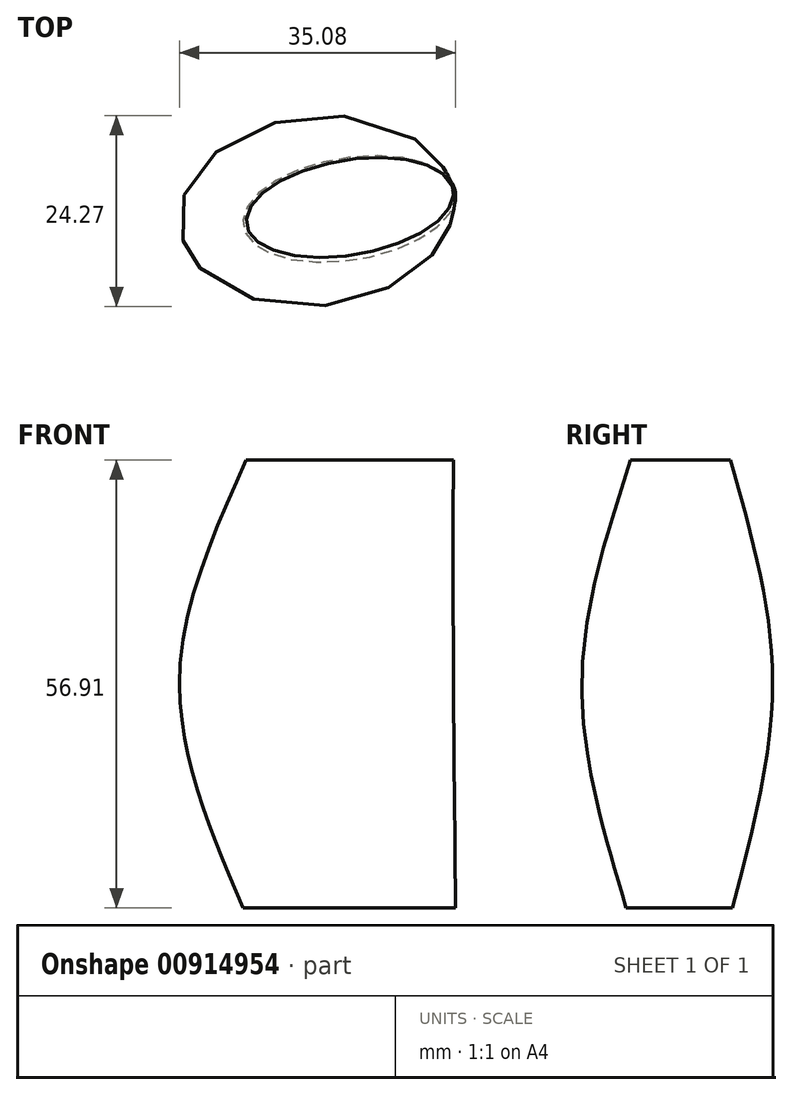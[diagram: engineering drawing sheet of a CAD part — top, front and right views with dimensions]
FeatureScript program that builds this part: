
annotation { "Feature Type Name" : "Feature", "Feature Type Description" : "" }
export const myFeature = defineFeature(function(context is Context, id is Id, definition is map)
    precondition{}
    {
        {
            var Q0;
            Q0=qCreatedBy(makeId("Front.planeOp"),FACE);
            var sketch = newSketch(context, id + "F0", { "sketchPlane" : qUnion([Q0])});
            skLineSegment(sketch, "E0", {"start": v(0, 69.9) * mm, "end": v(0, -51.9) * mm});
            skPoint(sketch, "E1", {"position": v(0, 56.91) * mm});
            skPoint(sketch, "E2", {"position": v(0, 0) * mm});
            skPoint(sketch, "E3", {"position": v(0, 29.5) * mm});
            skSolve(sketch);
        }
        {
            var Q0;
            Q0=qCreatedBy(makeId("Top.planeOp"),FACE);
            var sketch = newSketch(context, id + "F1", { "sketchPlane" : qUnion([Q0])});
            skEllipse(sketch, "E4", {"center": v(-10.4, 27.5) * mm, "majorRadius": 13.65 * mm, "minorRadius": 6.48 * mm, "majorAxis": v(0.99, 0.16)});
            skSolve(sketch);
        }
        {
            var Q0;
            Q0=sQuery(id+"F0.wireOp",VERTEX,"E3");
            var Q1;
            Q1=sQuery(id+"F0.wireOp",EDGE,"E0");
            cPlane(context, id + "F2", {"entities" : qUnion([Q0, Q1]), "cplaneType" : CPlaneType.CURVE_POINT, "offset" : 25.4 * mm, "width" : 152.4 * mm, "height" : 152.4 * mm});
        }
        {
            var Q0;
            Q0=sQuery(id+"F0.wireOp",VERTEX,"E1");
            var Q1;
            Q1=sQuery(id+"F0.wireOp",EDGE,"E0");
            cPlane(context, id + "F3", {"entities" : qUnion([Q0, Q1]), "cplaneType" : CPlaneType.CURVE_POINT, "offset" : 25.4 * mm, "width" : 152.4 * mm, "height" : 152.4 * mm});
        }
        {
            var Q0;
            Q0=qCreatedBy(id+"F2.planeOp",FACE);
            var sketch = newSketch(context, id + "F4", { "sketchPlane" : qUnion([Q0])});
            skEllipse(sketch, "E5", {"center": v(-14.56, -27.23) * mm, "majorRadius": 17.45 * mm, "minorRadius": 12.04 * mm, "majorAxis": v(1, -0.11)});
            skSolve(sketch);
        }
        {
            var Q0;
            Q0=qCreatedBy(id+"F3.planeOp",FACE);
            var sketch = newSketch(context, id + "F5", { "sketchPlane" : qUnion([Q0])});
            skEllipse(sketch, "E6", {"center": v(-10.33, -27.67) * mm, "majorRadius": 13.3 * mm, "minorRadius": 6.03 * mm, "majorAxis": v(0.99, -0.17)});
            skSolve(sketch);
        }
        {
            var Q0;
            Q0=makeQuery(id+"F5.imprint","IMPRINT",FACE,{"disambiguationData":[TD([[makeQuery(id+"F5.imprint","IMPRINT",EDGE,{"derivedFrom":sQuery(id+"F5.wireOp",EDGE,"E6")}),1.0]])]});
            var Q1;
            Q1=makeQuery(id+"F4.imprint","IMPRINT",FACE,{"disambiguationData":[TD([[makeQuery(id+"F4.imprint","IMPRINT",EDGE,{"derivedFrom":sQuery(id+"F4.wireOp",EDGE,"E5")}),1.0]])]});
            var Q2;
            Q2=makeQuery(id+"F1.imprint","IMPRINT",FACE,{"disambiguationData":[TD([[makeQuery(id+"F1.imprint","IMPRINT",EDGE,{"derivedFrom":sQuery(id+"F1.wireOp",EDGE,"E4")}),1.0]])]});
            loft(context, id + "F6", {"sheetProfilesArray" : [{ "sheetProfileEntities" : qUnion([Q0]) }, { "sheetProfileEntities" : qUnion([Q1]) }, { "sheetProfileEntities" : qUnion([Q2]) }]});
        }
    });
